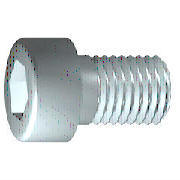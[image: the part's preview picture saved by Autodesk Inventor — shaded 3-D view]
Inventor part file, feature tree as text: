
AUTODESK INVENTOR PART (.ipt)
format: ipt  version: 2025 (Build 290162010, 162A)  size: 194,560 bytes
history: native  units: mm (DEFAULTED — no unit token found)
features: extrude x1, plane x1, fillet x1
ambient origin geometry x7: Origin, YZ Plane, XY Plane, X Axis, Y Axis, Z Axis, Center Point
bodies: Solid1 (feature_tree), Body (feature_tree)
feature tree (3):
  extrude  "Slot"  Depth=6.75mm
  plane  "Work Plane1"
  fillet  "Fillet2"  Radius=0.306825mm
